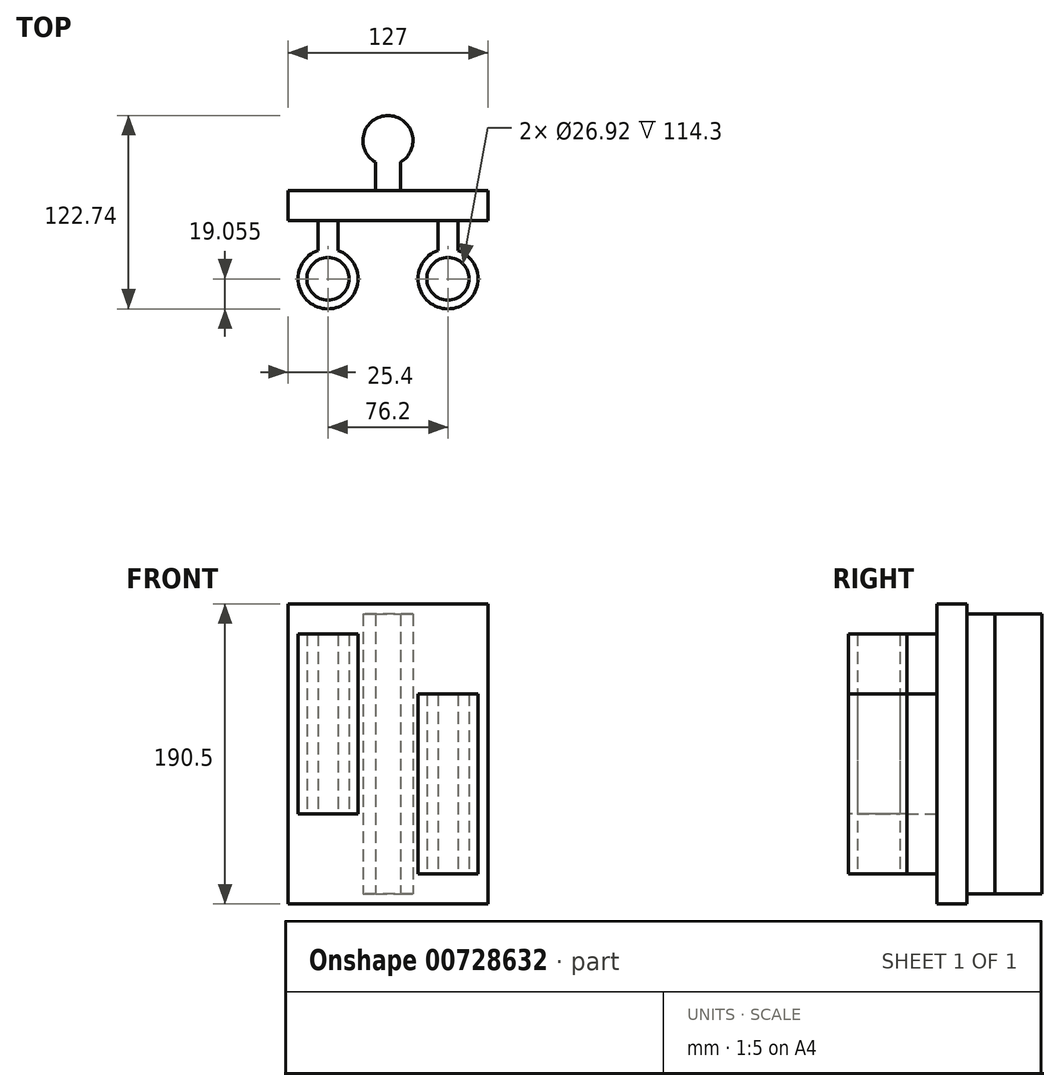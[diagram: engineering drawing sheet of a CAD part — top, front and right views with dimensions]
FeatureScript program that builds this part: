
annotation { "Feature Type Name" : "Feature", "Feature Type Description" : "" }
export const myFeature = defineFeature(function(context is Context, id is Id, definition is map)
    precondition{}
    {
        {
            var Q0;
            Q0=qCreatedBy(makeId("Front.planeOp"),FACE);
            var sketch = newSketch(context, id + "F0", { "sketchPlane" : qUnion([Q0])});
            skLineSegment(sketch, "E0.bottom", {"start": v(63.5, 95.25) * mm, "end": v(-63.5, 95.25) * mm});
            skLineSegment(sketch, "E0.top", {"start": v(63.5, -95.25) * mm, "end": v(-63.5, -95.25) * mm});
            skLineSegment(sketch, "E0.left", {"start": v(63.5, 95.25) * mm, "end": v(63.5, -95.25) * mm});
            skLineSegment(sketch, "E0.right", {"start": v(-63.5, 95.25) * mm, "end": v(-63.5, -95.25) * mm});
            skPoint(sketch, "E0.middle", {"position": v(0, 0) * mm});
            skSolve(sketch);
        }
        {
            var Q0;
            Q0=makeQuery(id+"F0.imprint","IMPRINT",FACE,{"disambiguationData":[TD([[makeQuery(id+"F0.imprint","IMPRINT",EDGE,{"derivedFrom":sQuery(id+"F0.wireOp",EDGE,"E0.bottom")}),1.0]])]});
            extrude(context, id + "F1", {"entities" : qUnion([Q0]), "endBound" : BoundingType.SYMMETRIC, "depth" : 19.05 * mm, "offsetDistance" : 25.4 * mm});
        }
        {
            var Q0;
            Q0=qCreatedBy(makeId("Top.planeOp"),FACE);
            var sketch = newSketch(context, id + "F2", { "sketchPlane" : qUnion([Q0])});
            skLineSegment(sketch, "E1", {"start": v(-44.45, -9.53) * mm, "end": v(-44.45, -28.57) * mm});
            skLineSegment(sketch, "E2", {"start": v(-31.75, -28.57) * mm, "end": v(-31.75, -9.53) * mm});
            skLineSegment(sketch, "E3", {"start": v(-44.45, -9.53) * mm, "end": v(-31.75, -9.53) * mm});
            skLineSegment(sketch, "E4", {"start": v(44.45, -9.52) * mm, "end": v(44.45, -28.58) * mm});
            skLineSegment(sketch, "E5", {"start": v(31.75, -9.53) * mm, "end": v(44.45, -9.53) * mm});
            skLineSegment(sketch, "E6", {"start": v(31.75, -9.52) * mm, "end": v(31.75, -28.58) * mm});
            skArc(sketch, "E7", {"start": v(31.75, -28.58) * mm, "mid": v(38.1, -65.59) * mm, "end": v(44.45, -28.57) * mm});
            skArc(sketch, "E8", {"start": v(-44.45, -28.58) * mm, "mid": v(-38.1, -65.59) * mm, "end": v(-31.75, -28.58) * mm});
            skLineSegment(sketch, "E9", {"start": v(-38.1, -46.54) * mm, "end": v(38.1, -46.54) * mm});
            skCircle(sketch, "E10", {"center": v(-38.1, -46.54) * mm, "radius": 13.46 * mm});
            skCircle(sketch, "E11", {"center": v(38.1, -46.54) * mm, "radius": 13.46 * mm});
            skLineSegment(sketch, "E12", {"start": v(38.1, -46.54) * mm, "end": v(38.1, -9.52) * mm});
            skLineSegment(sketch, "E13", {"start": v(-38.1, -46.54) * mm, "end": v(-38.1, -9.52) * mm});
            skSolve(sketch);
        }
        {
            var Q0;
            {var subQ6=sQuery(id+"F2.wireOp",EDGE,"E1");Q0=makeQuery(id+"F2.imprint","IMPRINT",FACE,{"disambiguationData":[TD([[makeQuery(id+"F2.imprint","IMPRINT",EDGE,{"derivedFrom":subQ6}),1.0]])]});}
            var Q1;
            {var subQ6=sQuery(id+"F2.wireOp",EDGE,"E2");Q1=makeQuery(id+"F2.imprint","IMPRINT",FACE,{"disambiguationData":[TD([[makeQuery(id+"F2.imprint","IMPRINT",EDGE,{"derivedFrom":subQ6}),1.0]])]});}
            extrude(context, id + "F3", {"entities" : qUnion([Q0, Q1]), "operationType" : NewBodyOperationType.ADD, "depth" : 76.2 * mm, "offsetDistance" : 25.4 * mm, "hasSecondDirection" : true, "secondDirectionOppositeDirection" : true, "secondDirectionDepth" : 38.1 * mm});
        }
        {
            var Q0;
            {var subQ1=sQuery(id+"F2.wireOp",EDGE,"E4");Q0=makeQuery(id+"F2.imprint","IMPRINT",FACE,{"disambiguationData":[TD([[makeQuery(id+"F2.imprint","IMPRINT",EDGE,{"derivedFrom":subQ1}),-1.0]])]});}
            var Q1;
            {var subQ5=sQuery(id+"F2.wireOp",EDGE,"E6");Q1=makeQuery(id+"F2.imprint","IMPRINT",FACE,{"disambiguationData":[TD([[makeQuery(id+"F2.imprint","IMPRINT",EDGE,{"derivedFrom":subQ5}),1.0]])]});}
            extrude(context, id + "F4", {"entities" : qUnion([Q0, Q1]), "operationType" : NewBodyOperationType.ADD, "depth" : 38.1 * mm, "offsetDistance" : 25.4 * mm, "hasSecondDirection" : true, "secondDirectionOppositeDirection" : true, "secondDirectionDepth" : 76.2 * mm});
        }
        {
            var Q0;
            Q0=qCreatedBy(makeId("Top.planeOp"),FACE);
            var sketch = newSketch(context, id + "F5", { "sketchPlane" : qUnion([Q0])});
            skLineSegment(sketch, "E14", {"start": v(-7.94, 9.53) * mm, "end": v(7.94, 9.53) * mm});
            skLineSegment(sketch, "E15", {"start": v(7.94, 9.53) * mm, "end": v(7.94, 27.53) * mm});
            skLineSegment(sketch, "E16", {"start": v(-7.94, 9.53) * mm, "end": v(-7.94, 27.53) * mm});
            skCircle(sketch, "E17", {"center": v(0, 41.27) * mm, "radius": 15.88 * mm});
            skLineSegment(sketch, "E18", {"start": v(0, 0) * mm, "end": v(0, 9.53) * mm});
            skSolve(sketch);
        }
        {
            var Q0;
            Q0 = qSketchRegion(id + "F5", true);
            extrude(context, id + "F6", {"entities" : qUnion([Q0]), "operationType" : NewBodyOperationType.ADD, "endBound" : BoundingType.SYMMETRIC, "depth" : 177.8 * mm, "offsetDistance" : 25.4 * mm});
        }
    });
